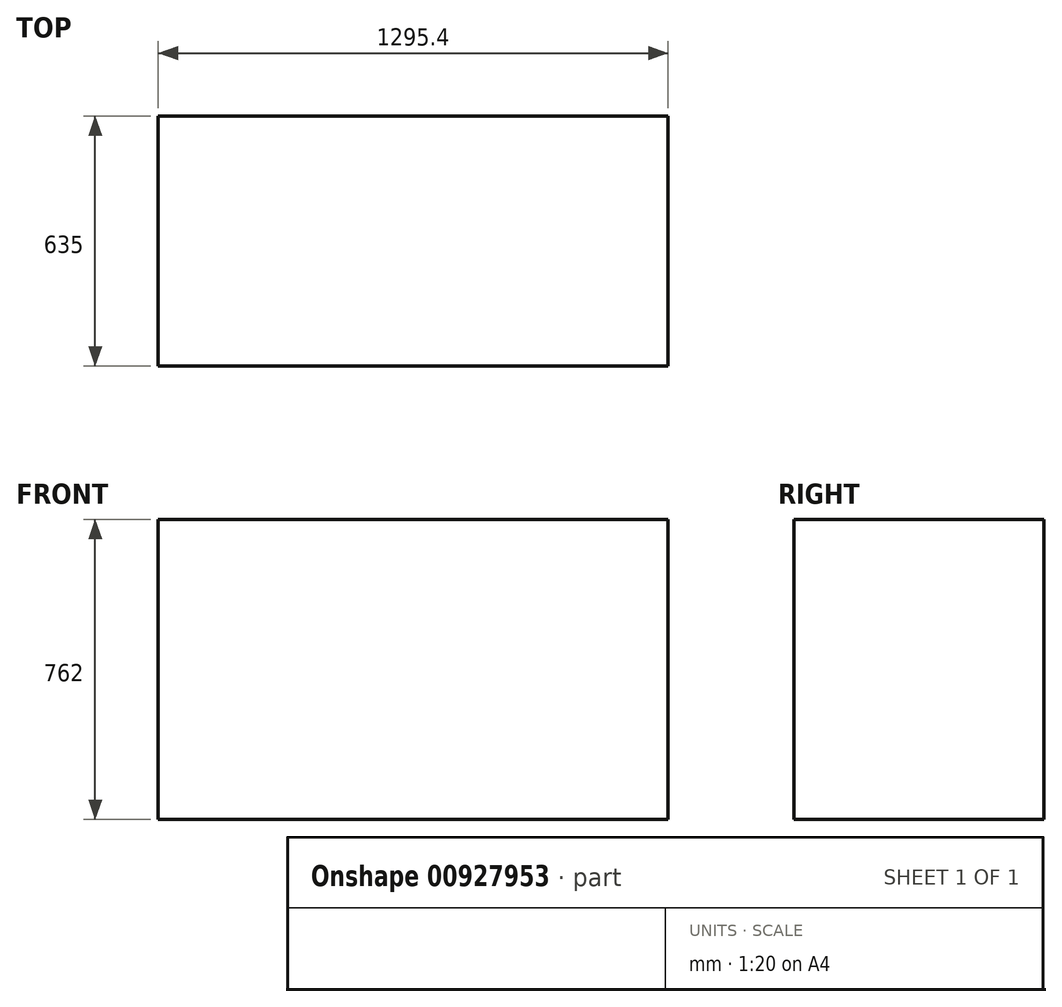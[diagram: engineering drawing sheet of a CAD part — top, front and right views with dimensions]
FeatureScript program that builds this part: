
annotation { "Feature Type Name" : "Feature", "Feature Type Description" : "" }
export const myFeature = defineFeature(function(context is Context, id is Id, definition is map)
    precondition{}
    {
        {
            var Q0;
            Q0=qCreatedBy(makeId("Top.planeOp"),FACE);
            var sketch = newSketch(context, id + "F0", { "sketchPlane" : qUnion([Q0])});
            skLineSegment(sketch, "E0.bottom", {"start": v(647.7, -317.5) * mm, "end": v(-647.7, -317.5) * mm});
            skLineSegment(sketch, "E0.top", {"start": v(647.7, 317.5) * mm, "end": v(-647.7, 317.5) * mm});
            skLineSegment(sketch, "E0.left", {"start": v(647.7, -317.5) * mm, "end": v(647.7, 317.5) * mm});
            skLineSegment(sketch, "E0.right", {"start": v(-647.7, -317.5) * mm, "end": v(-647.7, 317.5) * mm});
            skPoint(sketch, "E0.middle", {"position": v(0, 0) * mm});
            skSolve(sketch);
        }
        {
            var Q0;
            Q0 = qSketchRegion(id + "F0", true);
            extrude(context, id + "F1", {"entities" : qUnion([Q0]), "depth" : 762 * mm, "offsetDistance" : 25.4 * mm});
        }
    });
